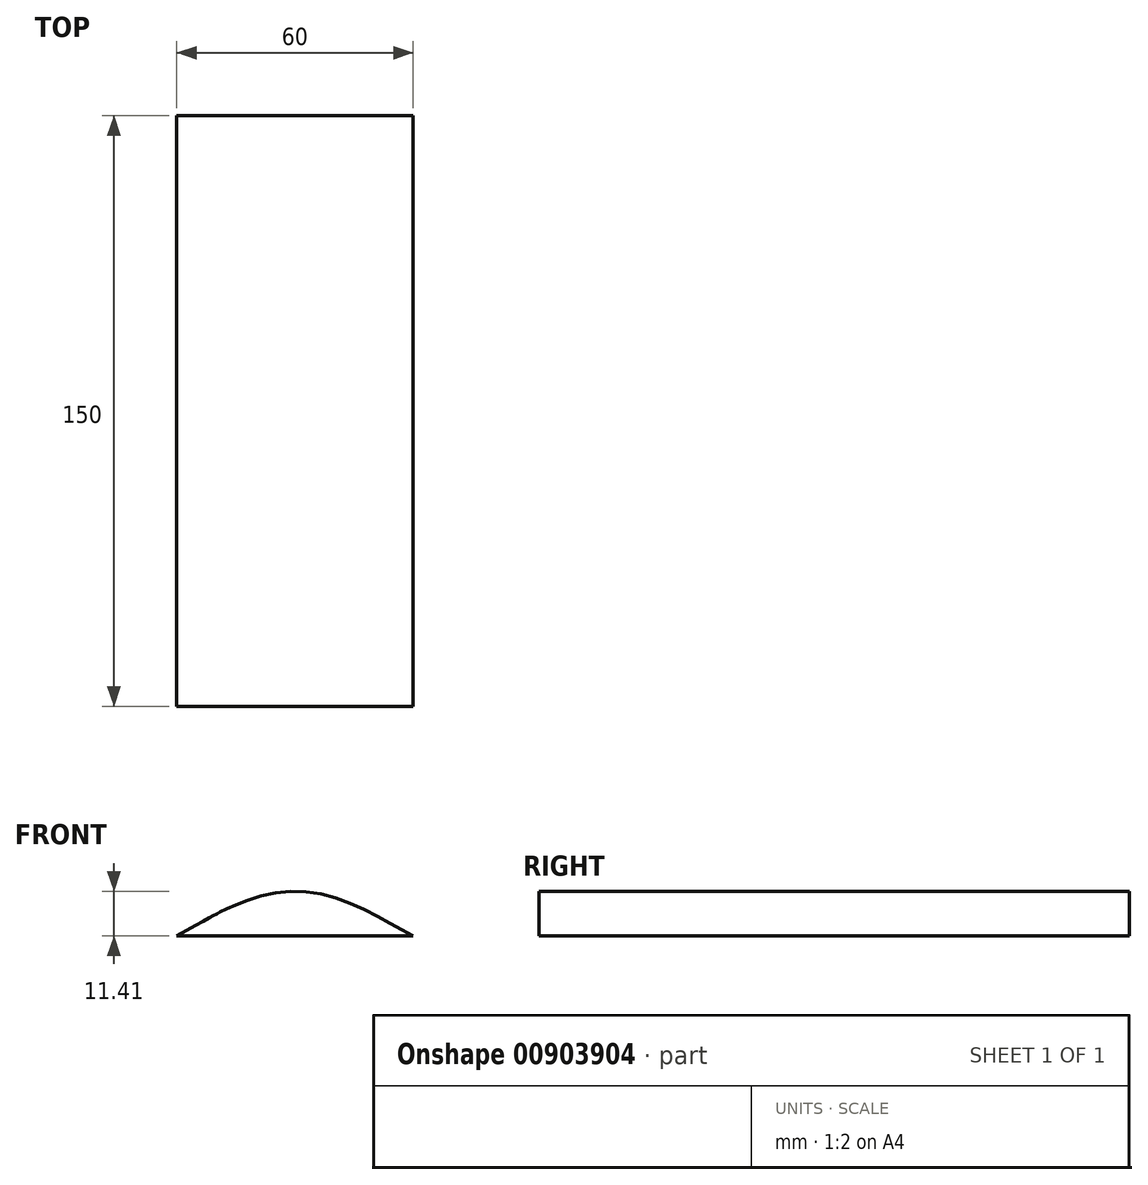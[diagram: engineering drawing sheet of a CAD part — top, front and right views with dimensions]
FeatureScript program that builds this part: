
annotation { "Feature Type Name" : "Feature", "Feature Type Description" : "" }
export const myFeature = defineFeature(function(context is Context, id is Id, definition is map)
    precondition{}
    {
        {
            var Q0;
            Q0=qCreatedBy(makeId("Front.planeOp"),FACE);
            var sketch = newSketch(context, id + "F0", { "sketchPlane" : qUnion([Q0])});
            skLineSegment(sketch, "E0", {"start": v(0, 0) * mm, "end": v(-29.47, 0) * mm});
            skLineSegment(sketch, "E1", {"start": v(0, 0) * mm, "end": v(30.53, 0) * mm});
            skFitSpline(sketch, "E2", {"points": [v(-29.47, 0) * mm, v(-20.06, 5.27) * mm, v(-19.45, 5.59) * mm, v(-19.2, 5.71) * mm, v(0, 11.4) * mm, v(30.53, 0) * mm], "startDerivative": vector(59.1, 34.29) * mm, "endDerivative": vector(60.89, -34.11) * mm});
            skSolve(sketch);
        }
        {
            var Q0;
            Q0 = qSketchRegion(id + "F0", true);
            extrude(context, id + "F1", {"entities" : qUnion([Q0]), "depth" : 150 * mm, "offsetDistance" : 25.4 * mm});
        }
    });
